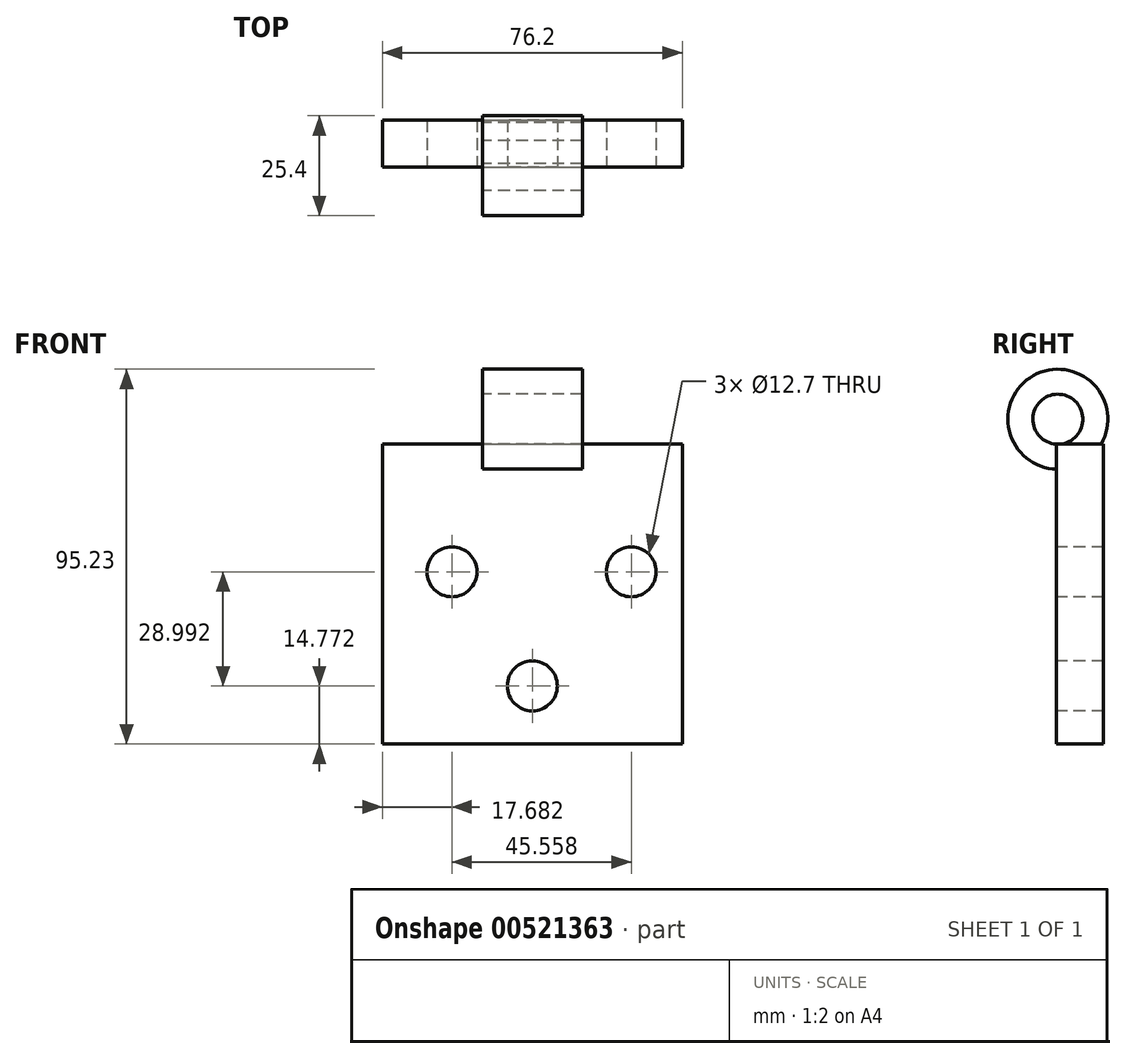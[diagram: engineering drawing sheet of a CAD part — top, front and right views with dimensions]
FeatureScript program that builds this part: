
annotation { "Feature Type Name" : "Feature", "Feature Type Description" : "" }
export const myFeature = defineFeature(function(context is Context, id is Id, definition is map)
    precondition{}
    {
        {
            var Q0;
            Q0=qCreatedBy(makeId("Front.planeOp"),FACE);
            var sketch = newSketch(context, id + "F0", { "sketchPlane" : qUnion([Q0])});
            skLineSegment(sketch, "E0.bottom", {"start": v(0, 0) * mm, "end": v(76.2, 0) * mm});
            skLineSegment(sketch, "E0.top", {"start": v(0, 76.2) * mm, "end": v(76.2, 76.2) * mm});
            skLineSegment(sketch, "E0.left", {"start": v(0, 0) * mm, "end": v(0, 76.2) * mm});
            skLineSegment(sketch, "E0.right", {"start": v(76.2, 0) * mm, "end": v(76.2, 76.2) * mm});
            skSolve(sketch);
        }
        {
            var Q0;
            Q0 = qSketchRegion(id + "F0", true);
            extrude(context, id + "F1", {"entities" : qUnion([Q0]), "depth" : 11.94 * mm, "offsetDistance" : 25.4 * mm});
        }
        {
            var Q0;
            Q0=makeQuery(id+"F1.opExtrude","SWEPT_FACE",FACE,{"disambiguationData":[OSD([sQuery(id+"F0.wireOp",EDGE,"E0.left")])]});
            var sketch = newSketch(context, id + "F2", { "sketchPlane" : qUnion([Q0])});
            skCircle(sketch, "E1", {"center": v(11.6, 82.53) * mm, "radius": 12.7 * mm});
            skCircle(sketch, "E2", {"center": v(11.6, 82.53) * mm, "radius": 6.35 * mm});
            skSolve(sketch);
        }
        {
            var Q0;
            Q0 = qSketchRegion(id + "F2", true);
            extrude(context, id + "F3", {"entities" : qUnion([Q0]), "operationType" : NewBodyOperationType.ADD, "oppositeDirection" : true, "depth" : 50.8 * mm, "offsetDistance" : 25.4 * mm, "hasSecondDirection" : true, "secondDirectionOppositeDirection" : true, "secondDirectionDepth" : 25.4 * mm});
        }
        {
            var Q0;
            Q0=makeQuery(id+"F1.opExtrude","CAP_FACE",FACE,{"disambiguationData":[OSD([sQuery(id+"F0.wireOp",EDGE,"E0.bottom"),sQuery(id+"F0.wireOp",EDGE,"E0.top"),sQuery(id+"F0.wireOp",EDGE,"E0.left"),sQuery(id+"F0.wireOp",EDGE,"E0.right")])],"isStart":false});
            var sketch = newSketch(context, id + "F4", { "sketchPlane" : qUnion([Q0])});
            skCircle(sketch, "E3", {"center": v(38.1, 14.77) * mm, "radius": 6.35 * mm});
            skPoint(sketch, "E3.centerSnap0", {"position": v(38.1, 69.84) * mm});
            skCircle(sketch, "E4", {"center": v(17.68, 43.76) * mm, "radius": 6.35 * mm});
            skCircle(sketch, "E5", {"center": v(63.24, 43.76) * mm, "radius": 6.35 * mm});
            skSolve(sketch);
        }
        {
            var Q0;
            Q0 = qSketchRegion(id + "F4", true);
            extrude(context, id + "F5", {"entities" : qUnion([Q0]), "operationType" : NewBodyOperationType.REMOVE, "oppositeDirection" : true, "depth" : 25.4 * mm, "offsetDistance" : 25.4 * mm});
        }
    });
